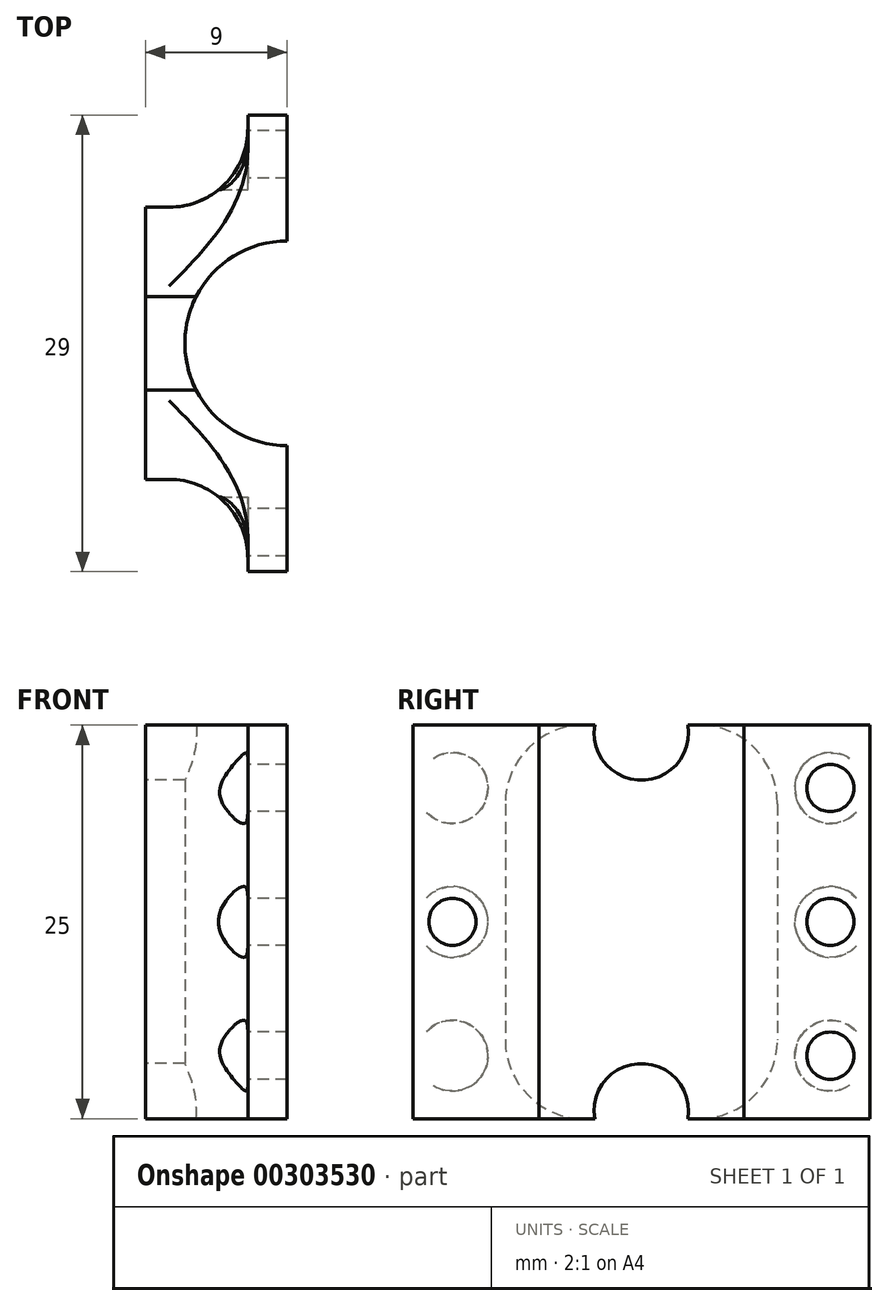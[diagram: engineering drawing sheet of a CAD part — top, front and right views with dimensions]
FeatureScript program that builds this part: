
annotation { "Feature Type Name" : "Feature", "Feature Type Description" : "" }
export const myFeature = defineFeature(function(context is Context, id is Id, definition is map)
    precondition{}
    {
        {
            var Q0;
            Q0=qCreatedBy(makeId("Top.planeOp"),FACE);
            var sketch = newSketch(context, id + "F0", { "sketchPlane" : qUnion([Q0])});
            skLineSegment(sketch, "E0", {"start": v(-13.6, 14.5) * mm, "end": v(-13.6, 6.5) * mm});
            skPoint(sketch, "E1", {"position": v(-13.6, 0) * mm});
            skArc(sketch, "E2", {"start": v(-13.6, 6.5) * mm, "mid": v(-20.1, 0) * mm, "end": v(-13.6, -6.5) * mm});
            skLineSegment(sketch, "E3.trimOffspring", {"start": v(-13.6, -6.5) * mm, "end": v(-13.6, -14.5) * mm});
            skLineSegment(sketch, "E4.0", {"start": v(-16.1, -8.65) * mm, "end": v(-16.1, -14.5) * mm});
            skLineSegment(sketch, "E4.2", {"start": v(-16.1, 14.5) * mm, "end": v(-16.1, 8.65) * mm});
            skLineSegment(sketch, "E5", {"start": v(-13.6, 14.5) * mm, "end": v(-16.1, 14.5) * mm});
            skLineSegment(sketch, "E6", {"start": v(-13.6, -14.5) * mm, "end": v(-16.1, -14.5) * mm});
            skLineSegment(sketch, "E7", {"start": v(-16.1, 8.65) * mm, "end": v(-22.6, 8.65) * mm});
            skLineSegment(sketch, "E8", {"start": v(-22.6, 8.65) * mm, "end": v(-22.6, -8.65) * mm});
            skLineSegment(sketch, "E9", {"start": v(-22.6, -8.65) * mm, "end": v(-16.1, -8.65) * mm});
            skSolve(sketch);
        }
        {
            var Q0;
            Q0=makeQuery(id+"F0.imprint","IMPRINT",FACE,{"disambiguationData":[TD([[makeQuery(id+"F0.imprint","IMPRINT",EDGE,{"derivedFrom":sQuery(id+"F0.wireOp",EDGE,"E0")}),-1.0]])]});
            extrude(context, id + "F1", {"entities" : qUnion([Q0]), "depth" : 25 * mm});
        }
        {
            var Q0;
            Q0=makeQuery(id+"F1.opExtrude","SWEPT_FACE",FACE,{"disambiguationData":[OSD([sQuery(id+"F0.wireOp",EDGE,"E8")])]});
            var sketch = newSketch(context, id + "F2", { "sketchPlane" : qUnion([Q0])});
            skLineSegment(sketch, "E10", {"start": v(0, 25) * mm, "end": v(0, 24.5) * mm, "construction": true});
            skPoint(sketch, "E10.endSnap0", {"position": v(0, 25) * mm});
            skLineSegment(sketch, "E11", {"start": v(0, 0) * mm, "end": v(0, 0.5) * mm, "construction": true});
            skCircle(sketch, "E12", {"center": v(0, 24.5) * mm, "radius": 3 * mm});
            skCircle(sketch, "E13", {"center": v(0, 0.5) * mm, "radius": 3 * mm});
            skLineSegment(sketch, "E14", {"start": v(0, 25) * mm, "end": v(0, 0) * mm, "construction": true});
            skCircle(sketch, "E15", {"center": v(0, 12.5) * mm, "radius": 12 * mm, "construction": true});
            skCircle(sketch, "E16", {"center": v(12, 12.5) * mm, "radius": 1.5 * mm});
            skPoint(sketch, "E16.centerSnap0", {"position": v(8.65, 12.5) * mm});
            skLineSegment(sketch, "E17", {"start": v(0, 12.5) * mm, "end": v(-12, 12.5) * mm, "construction": true});
            skLineSegment(sketch, "E18", {"start": v(0, 12.5) * mm, "end": v(12, 12.5) * mm, "construction": true});
            skCircle(sketch, "E19", {"center": v(-12, 12.5) * mm, "radius": 1.5 * mm});
            skPoint(sketch, "E20", {"position": v(-12, 21) * mm});
            skPoint(sketch, "E21", {"position": v(-12, 4) * mm});
            skPoint(sketch, "E22.trimOffspring.end.orphan", {"position": v(-12, 0) * mm});
            skPoint(sketch, "E23.start.orphan", {"position": v(-12, 25) * mm});
            skLineSegment(sketch, "E24", {"start": v(-12, 12.5) * mm, "end": v(-12, 21) * mm, "construction": true});
            skLineSegment(sketch, "E25", {"start": v(-12, 12.5) * mm, "end": v(-12, 4) * mm, "construction": true});
            skCircle(sketch, "E26", {"center": v(-12, 21) * mm, "radius": 1.5 * mm});
            skCircle(sketch, "E27", {"center": v(-12, 4) * mm, "radius": 1.5 * mm});
            skCircle(sketch, "E28.MirrorC", {"center": v(12, 4) * mm, "radius": 1.5 * mm});
            skCircle(sketch, "E29.MirrorC", {"center": v(12, 21) * mm, "radius": 1.5 * mm});
            skSolve(sketch);
        }
        {
            var Q0;
            {var subQ0=sQuery(id+"F2.wireOp",EDGE,"E12");var subQ1=makeQuery(id+"F1.opExtrude","CAP_EDGE",EDGE,{"disambiguationData":[OSD([sQuery(id+"F0.wireOp",EDGE,"E8")])],"isStart":false});var subQ2=makeQuery(id+"F2.imprint","INTERSECT",VERTEX,{"disambiguationData":[OD(0.0)],"derivedFrom":[subQ1,subQ0]});Q0=makeQuery(id+"F2.imprint","IMPRINT",FACE,{"disambiguationData":[TD([[makeQuery(id+"F2.imprint","IMPRINT",EDGE,{"disambiguationData":[TD([[subQ2,-1.0]])],"derivedFrom":subQ0}),1.0]])]});}
            var Q1;
            {var subQ0=sQuery(id+"F2.wireOp",EDGE,"E13");var subQ1=makeQuery(id+"F1.opExtrude","CAP_EDGE",EDGE,{"disambiguationData":[OSD([sQuery(id+"F0.wireOp",EDGE,"E8")])],"isStart":true});var subQ2=makeQuery(id+"F2.imprint","INTERSECT",VERTEX,{"disambiguationData":[OD(0.0)],"derivedFrom":[subQ1,subQ0]});Q1=makeQuery(id+"F2.imprint","IMPRINT",FACE,{"disambiguationData":[TD([[makeQuery(id+"F2.imprint","IMPRINT",EDGE,{"disambiguationData":[TD([[subQ2,1.0]])],"derivedFrom":subQ0}),1.0]])]});}
            var Q2;
            Q2=makeQuery(id+"F2.imprint","IMPRINT",FACE,{"disambiguationData":[TD([[makeQuery(id+"F2.imprint","IMPRINT",EDGE,{"derivedFrom":sQuery(id+"F2.wireOp",EDGE,"E19")}),1.0]])]});
            var Q3;
            Q3=makeQuery(id+"F2.imprint","IMPRINT",FACE,{"disambiguationData":[TD([[makeQuery(id+"F2.imprint","IMPRINT",EDGE,{"derivedFrom":sQuery(id+"F2.wireOp",EDGE,"E16")}),1.0]])]});
            var Q4;
            Q4=makeQuery(id+"F2.imprint","IMPRINT",FACE,{"disambiguationData":[TD([[makeQuery(id+"F2.imprint","IMPRINT",EDGE,{"derivedFrom":sQuery(id+"F2.wireOp",EDGE,"E26")}),1.0]])]});
            var Q5;
            Q5=makeQuery(id+"F2.imprint","IMPRINT",FACE,{"disambiguationData":[TD([[makeQuery(id+"F2.imprint","IMPRINT",EDGE,{"derivedFrom":sQuery(id+"F2.wireOp",EDGE,"E27")}),1.0]])]});
            var Q6;
            Q6=makeQuery(id+"F2.imprint","IMPRINT",FACE,{"disambiguationData":[TD([[makeQuery(id+"F2.imprint","IMPRINT",EDGE,{"derivedFrom":sQuery(id+"F2.wireOp",EDGE,"E29.MirrorC")}),-1.0]])]});
            var Q7;
            Q7=makeQuery(id+"F2.imprint","IMPRINT",FACE,{"disambiguationData":[TD([[makeQuery(id+"F2.imprint","IMPRINT",EDGE,{"derivedFrom":sQuery(id+"F2.wireOp",EDGE,"E28.MirrorC")}),-1.0]])]});
            extrude(context, id + "F3", {"entities" : qUnion([Q0, Q1, Q2, Q3, Q4, Q5, Q6, Q7]), "operationType" : NewBodyOperationType.REMOVE, "endBound" : BoundingType.THROUGH_ALL, "oppositeDirection" : true, "depth" : 5 * mm});
        }
        {
            var Q0;
            Q0=makeQuery(id+"F1.opExtrude","CAP_EDGE",EDGE,{"disambiguationData":[OSD([sQuery(id+"F0.wireOp",EDGE,"E9")])],"isStart":false});
            var Q1;
            Q1=makeQuery(id+"F1.opExtrude","CAP_EDGE",EDGE,{"disambiguationData":[OSD([sQuery(id+"F0.wireOp",EDGE,"E7")])],"isStart":false});
            var Q2;
            Q2=makeQuery(id+"F1.opExtrude","CAP_EDGE",EDGE,{"disambiguationData":[OSD([sQuery(id+"F0.wireOp",EDGE,"E7")])],"isStart":true});
            var Q3;
            Q3=makeQuery(id+"F1.opExtrude","CAP_EDGE",EDGE,{"disambiguationData":[OSD([sQuery(id+"F0.wireOp",EDGE,"E9")])],"isStart":true});
            fillet(context, id + "F4", {"entities" : qUnion([Q0, Q1, Q2, Q3]), "radius" : 5 * mm, "tangentPropagation" : true, "allowEdgeOverflow" : false});
        }
        {
            var Q0;
            Q0=makeQuery(id+"F1.opExtrude","SWEPT_EDGE",EDGE,{"disambiguationData":[OSD([sQuery(id+"F0.wireOp",EDGE,"E4.2"),sQuery(id+"F0.wireOp",EDGE,"E7")])]});
            var Q1;
            Q1=makeQuery(id+"F1.opExtrude","SWEPT_EDGE",EDGE,{"disambiguationData":[OSD([sQuery(id+"F0.wireOp",EDGE,"E4.0"),sQuery(id+"F0.wireOp",EDGE,"E9")])]});
            fillet(context, id + "F5", {"entities" : qUnion([Q0, Q1]), "radius" : 5 * mm, "tangentPropagation" : true, "allowEdgeOverflow" : false});
        }
        {
            var Q0;
            Q0=makeQuery(id+"F1.opExtrude","SWEPT_FACE",FACE,{"disambiguationData":[OSD([sQuery(id+"F0.wireOp",EDGE,"E4.2")])]});
            var sketch = newSketch(context, id + "F6", { "sketchPlane" : qUnion([Q0])});
            skCircle(sketch, "E30", {"center": v(12, 4) * mm, "radius": 2.25 * mm});
            skCircle(sketch, "E31", {"center": v(12, 12.5) * mm, "radius": 2.25 * mm});
            skCircle(sketch, "E32", {"center": v(12, 21) * mm, "radius": 2.25 * mm});
            skCircle(sketch, "E33.MirrorC", {"center": v(-12, 4) * mm, "radius": 2.25 * mm});
            skCircle(sketch, "E34.MirrorC", {"center": v(-12, 12.5) * mm, "radius": 2.25 * mm});
            skCircle(sketch, "E35.MirrorC", {"center": v(-12, 21) * mm, "radius": 2.25 * mm});
            skSolve(sketch);
        }
        {
            var Q0;
            Q0 = qSketchRegion(id + "F6", true);
            extrude(context, id + "F7", {"entities" : qUnion([Q0]), "operationType" : NewBodyOperationType.REMOVE, "depth" : 25 * mm});
        }
    });
